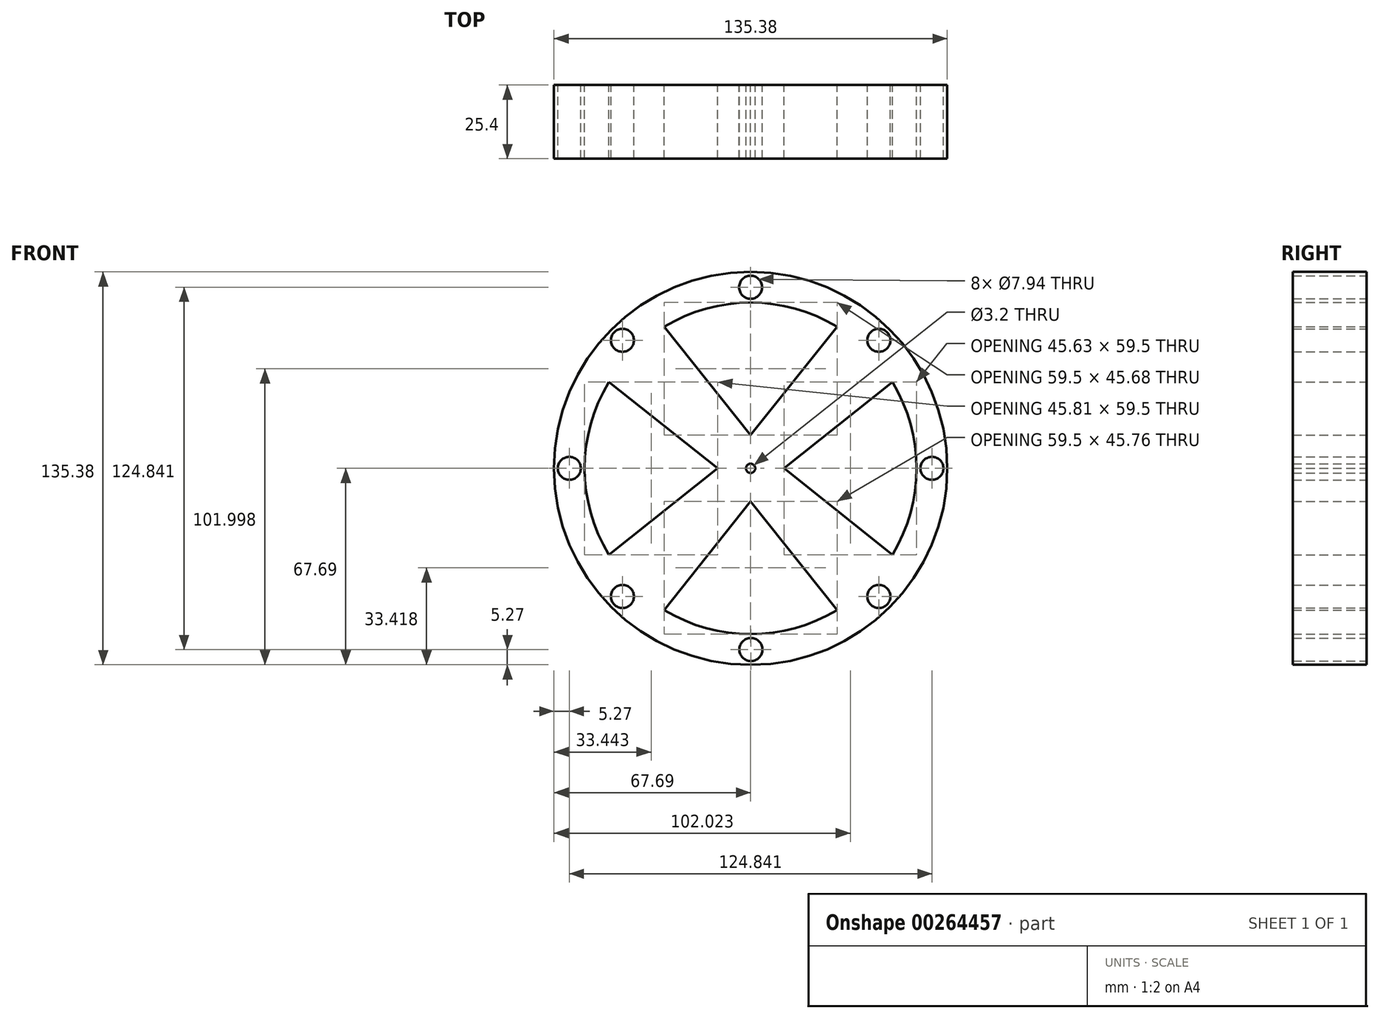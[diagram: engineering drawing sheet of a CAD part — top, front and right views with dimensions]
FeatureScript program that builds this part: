
annotation { "Feature Type Name" : "Feature", "Feature Type Description" : "" }
export const myFeature = defineFeature(function(context is Context, id is Id, definition is map)
    precondition{}
    {
        {
            var Q0;
            Q0=qCreatedBy(makeId("Front.planeOp"),FACE);
            var sketch = newSketch(context, id + "F0", { "sketchPlane" : qUnion([Q0])});
            skCircle(sketch, "E0", {"center": v(0, 0) * mm, "radius": 1.6 * mm});
            skCircle(sketch, "E1", {"center": v(0, 0) * mm, "radius": 67.7 * mm});
            skArc(sketch, "E2", {"start": v(-48.8, 29.75) * mm, "mid": v(-57.15, 0) * mm, "end": v(-48.8, -29.75) * mm});
            skLineSegment(sketch, "E3", {"start": v(0, 11.47) * mm, "end": v(-29.75, 48.8) * mm});
            skLineSegment(sketch, "E4", {"start": v(0, 11.47) * mm, "end": v(29.75, 48.8) * mm});
            skLineSegment(sketch, "E5", {"start": v(11.52, 0) * mm, "end": v(48.8, -29.75) * mm});
            skLineSegment(sketch, "E6", {"start": v(11.52, 0) * mm, "end": v(48.8, 29.75) * mm});
            skLineSegment(sketch, "E7", {"start": v(0, -11.4) * mm, "end": v(-29.75, -48.8) * mm});
            skLineSegment(sketch, "E8", {"start": v(0, -11.4) * mm, "end": v(29.75, -48.8) * mm});
            skLineSegment(sketch, "E9", {"start": v(-11.34, 0) * mm, "end": v(-48.8, 29.75) * mm});
            skLineSegment(sketch, "E10", {"start": v(-11.34, 0) * mm, "end": v(-48.8, -29.75) * mm});
            skArc(sketch, "E11.trimOffspring", {"start": v(48.8, -29.75) * mm, "mid": v(57.15, 0) * mm, "end": v(48.8, 29.75) * mm});
            skArc(sketch, "E12.trimOffspring", {"start": v(29.75, 48.8) * mm, "mid": v(0, 57.15) * mm, "end": v(-29.75, 48.8) * mm});
            skArc(sketch, "E13.trimOffspring", {"start": v(-29.75, -48.8) * mm, "mid": v(0, -57.15) * mm, "end": v(29.75, -48.8) * mm});
            skLineSegment(sketch, "E14", {"start": v(0, 0) * mm, "end": v(0.09, 0.04) * mm, "construction": true});
            skCircle(sketch, "E15", {"center": v(0, 0) * mm, "radius": 57.15 * mm});
            skLineSegment(sketch, "E16", {"start": v(0.09, 0.04) * mm, "end": v(0, -11.4) * mm, "construction": true});
            skLineSegment(sketch, "E17", {"start": v(0, 11.47) * mm, "end": v(0.09, 0.04) * mm, "construction": true});
            skLineSegment(sketch, "E18", {"start": v(-11.34, 0) * mm, "end": v(0.09, 0.04) * mm, "construction": true});
            skLineSegment(sketch, "E19", {"start": v(0.09, 0.04) * mm, "end": v(11.52, 0) * mm, "construction": true});
            skPoint(sketch, "E20.startSnap0", {"position": v(5.8, 0.02) * mm});
            skPoint(sketch, "E21.startSnap0", {"position": v(-5.63, 0.02) * mm});
            skPoint(sketch, "E22.orphan", {"position": v(39.27, -39.27) * mm});
            skPoint(sketch, "E23.orphan", {"position": v(-39.27, -39.27) * mm});
            skPoint(sketch, "E24.orphan", {"position": v(39.27, 39.27) * mm});
            skCircle(sketch, "E25", {"center": v(-62.42, 0.02) * mm, "radius": 3.97 * mm});
            skPoint(sketch, "E25.centerSnap0", {"position": v(-62.42, 0.03) * mm});
            skCircle(sketch, "E26", {"center": v(-44.14, 44.14) * mm, "radius": 3.97 * mm});
            skCircle(sketch, "E27", {"center": v(0, 62.42) * mm, "radius": 3.97 * mm});
            skCircle(sketch, "E28", {"center": v(44.14, 44.14) * mm, "radius": 3.97 * mm});
            skCircle(sketch, "E29", {"center": v(62.42, 0.02) * mm, "radius": 3.97 * mm});
            skCircle(sketch, "E30", {"center": v(44.14, -44.14) * mm, "radius": 3.97 * mm});
            skCircle(sketch, "E31", {"center": v(0.09, -62.42) * mm, "radius": 3.97 * mm});
            skCircle(sketch, "E32", {"center": v(-44.14, -44.14) * mm, "radius": 3.97 * mm});
            skPoint(sketch, "E33.orphan", {"position": v(-47.86, 47.86) * mm});
            skPoint(sketch, "E34.start.orphan", {"position": v(-40.41, 40.41) * mm});
            skPoint(sketch, "E35.orphan", {"position": v(0, 57.15) * mm});
            skPoint(sketch, "E36.end.orphan", {"position": v(0, 67.7) * mm});
            skPoint(sketch, "E37.start.orphan", {"position": v(40.41, 40.41) * mm});
            skPoint(sketch, "E38.trimOffspring.end.orphan", {"position": v(47.86, 47.86) * mm});
            skPoint(sketch, "E39.trimOffspring.end.orphan", {"position": v(-67.7, 0.05) * mm});
            skPoint(sketch, "E21.start.orphan", {"position": v(-57.15, 0.02) * mm});
            skPoint(sketch, "E20.start.orphan", {"position": v(57.15, 0.02) * mm});
            skPoint(sketch, "E40.trimOffspring.end.orphan", {"position": v(67.7, 0.02) * mm});
            skPoint(sketch, "E41.orphan", {"position": v(0.09, -57.15) * mm});
            skPoint(sketch, "E42.end.orphan", {"position": v(0.09, -67.7) * mm});
            skPoint(sketch, "E43.orphan", {"position": v(47.86, -47.86) * mm});
            skPoint(sketch, "E44.start.orphan", {"position": v(40.41, -40.41) * mm});
            skPoint(sketch, "E45.orphan", {"position": v(-40.41, -40.41) * mm});
            skPoint(sketch, "E46.end.orphan", {"position": v(-47.86, -47.86) * mm});
            skSolve(sketch);
        }
        {
            var Q0;
            Q0=makeQuery(id+"F0.imprint","IMPRINT",FACE,{"disambiguationData":[TD([[makeQuery(id+"F0.imprint","IMPRINT",EDGE,{"derivedFrom":sQuery(id+"F0.wireOp",EDGE,"E0")}),-1.0]])]});
            var Q1;
            Q1=makeQuery(id+"F0.imprint","IMPRINT",FACE,{"disambiguationData":[TD([[makeQuery(id+"F0.imprint","IMPRINT",EDGE,{"derivedFrom":sQuery(id+"F0.wireOp",EDGE,"E1")}),1.0]])]});
            extrude(context, id + "F1", {"entities" : qUnion([Q0, Q1]), "depth" : 25.4 * mm});
        }
    });
